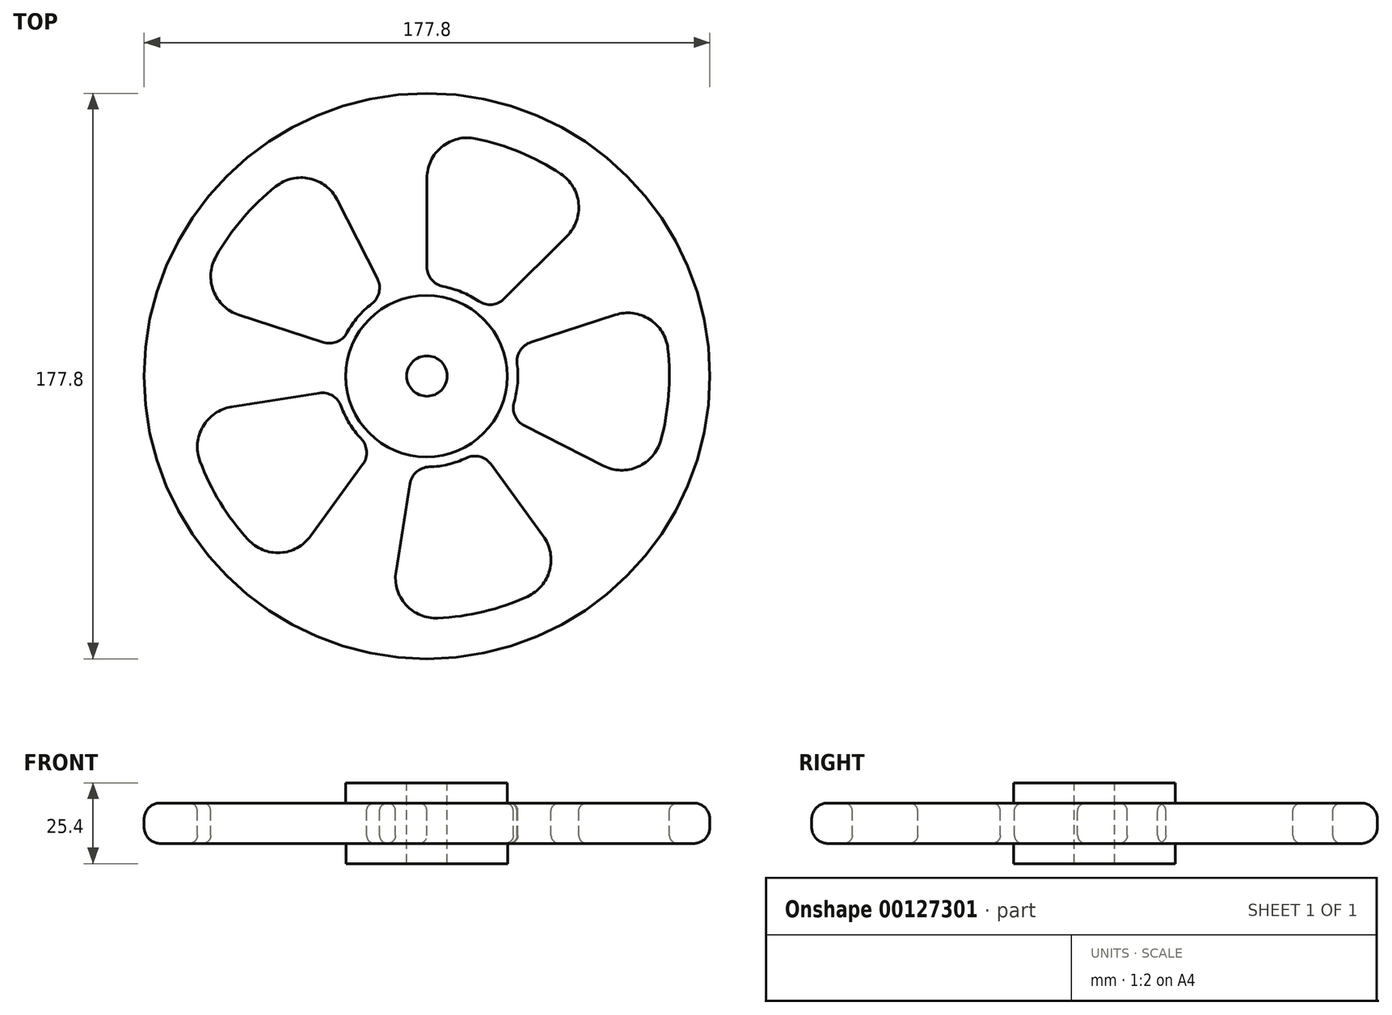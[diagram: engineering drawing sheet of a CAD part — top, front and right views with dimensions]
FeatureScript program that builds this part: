
annotation { "Feature Type Name" : "Feature", "Feature Type Description" : "" }
export const myFeature = defineFeature(function(context is Context, id is Id, definition is map)
    precondition{}
    {
        {
            var Q0;
            Q0=qCreatedBy(makeId("Top.planeOp"),FACE);
            var sketch = newSketch(context, id + "F0", { "sketchPlane" : qUnion([Q0])});
            skCircle(sketch, "E0", {"center": v(0, 0) * mm, "radius": 88.9 * mm});
            skSolve(sketch);
        }
        {
            var Q0;
            Q0 = qSketchRegion(id + "F0", true);
            extrude(context, id + "F1", {"entities" : qUnion([Q0]), "depth" : 12.7 * mm});
        }
        {
            var Q0;
            Q0=makeQuery(id+"F1.opExtrude","CAP_FACE",FACE,{"disambiguationData":[OSD([sQuery(id+"F0.wireOp",EDGE,"E0")])],"isStart":false});
            var sketch = newSketch(context, id + "F2", { "sketchPlane" : qUnion([Q0])});
            skCircle(sketch, "E1", {"center": v(-0.17, -0.07) * mm, "radius": 25.4 * mm});
            skSolve(sketch);
        }
        {
            var Q0;
            Q0 = qSketchRegion(id + "F2", true);
            extrude(context, id + "F3", {"entities" : qUnion([Q0]), "operationType" : NewBodyOperationType.ADD, "depth" : 6.35 * mm});
        }
        {
            var Q0;
            Q0=makeQuery(id+"F1.opExtrude","CAP_FACE",FACE,{"disambiguationData":[OSD([sQuery(id+"F0.wireOp",EDGE,"E0")])],"isStart":true});
            var sketch = newSketch(context, id + "F4", { "sketchPlane" : qUnion([Q0])});
            skCircle(sketch, "E2", {"center": v(0, 0) * mm, "radius": 25.4 * mm});
            skSolve(sketch);
        }
        {
            var Q0;
            Q0 = qSketchRegion(id + "F4", true);
            var Q1;
            Q1=makeQuery(id+"F4.imprint","IMPRINT",FACE,{"disambiguationData":[TD([[makeQuery(id+"F4.imprint","IMPRINT",EDGE,{"derivedFrom":sQuery(id+"F4.wireOp",EDGE,"E2")}),1.0]])]});
            extrude(context, id + "F5", {"entities" : qUnion([Q0, Q1]), "operationType" : NewBodyOperationType.ADD, "depth" : 6.35 * mm});
        }
        {
            var Q0;
            Q0=makeQuery(id+"F3.opExtrude","CAP_FACE",FACE,{"disambiguationData":[OSD([sQuery(id+"F2.wireOp",EDGE,"E1")])],"isStart":false});
            var sketch = newSketch(context, id + "F6", { "sketchPlane" : qUnion([Q0])});
            skArc(sketch, "E3", {"start": v(16.2, 23.54) * mm, "mid": v(10.94, 26.4) * mm, "end": v(5.2, 28.1) * mm});
            skArc(sketch, "E4", {"start": v(42.02, 63.57) * mm, "mid": v(29.16, 70.4) * mm, "end": v(15.24, 74.66) * mm});
            skLineSegment(sketch, "E5", {"start": v(0, 0) * mm, "end": v(0, 83.16) * mm, "construction": true});
            skLineSegment(sketch, "E6", {"start": v(0, 0) * mm, "end": v(59.56, 59.56) * mm, "construction": true});
            skLineSegment(sketch, "E7", {"start": v(0, 0) * mm, "end": v(80.55, 0) * mm, "construction": true});
            skLineSegment(sketch, "E8", {"start": v(24.28, 24.28) * mm, "end": v(44, 44) * mm});
            skLineSegment(sketch, "E9", {"start": v(0, 34.34) * mm, "end": v(0, 62.22) * mm});
            skPoint(sketch, "E10.visualSharp", {"position": v(0, 76.2) * mm});
            skArc(sketch, "E10.filletArc", {"start": v(15.24, 74.66) * mm, "mid": v(4.67, 72.05) * mm, "end": v(0, 62.22) * mm});
            skPoint(sketch, "E11.visualSharp", {"position": v(53.88, 53.88) * mm});
            skArc(sketch, "E11.filletArc", {"start": v(44, 44) * mm, "mid": v(47.65, 54.25) * mm, "end": v(42.02, 63.57) * mm});
            skPoint(sketch, "E12.visualSharp", {"position": v(0, 28.58) * mm});
            skArc(sketch, "E12.filletArc", {"start": v(0, 34.34) * mm, "mid": v(1.47, 30.28) * mm, "end": v(5.2, 28.1) * mm});
            skPoint(sketch, "E13.visualSharp", {"position": v(20.2, 20.2) * mm});
            skArc(sketch, "E13.filletArc", {"start": v(16.2, 23.54) * mm, "mid": v(20.37, 22.45) * mm, "end": v(24.28, 24.28) * mm});
            skLineSegment(sketch, "E14.1.0", {"start": v(-15.6, 30.6) * mm, "end": v(-28.25, 55.44) * mm});
            skArc(sketch, "E14.1.1", {"start": v(-28.25, 55.44) * mm, "mid": v(-36.87, 62.08) * mm, "end": v(-47.47, 59.6) * mm});
            skArc(sketch, "E14.1.2", {"start": v(-47.47, 59.6) * mm, "mid": v(-57.94, 49.49) * mm, "end": v(-66.3, 37.57) * mm});
            skArc(sketch, "E14.1.3", {"start": v(-66.3, 37.57) * mm, "mid": v(-67.09, 26.7) * mm, "end": v(-59.17, 19.23) * mm});
            skLineSegment(sketch, "E14.1.4", {"start": v(-32.66, 10.61) * mm, "end": v(-59.17, 19.23) * mm});
            skArc(sketch, "E14.1.5", {"start": v(-32.66, 10.61) * mm, "mid": v(-28.35, 10.75) * mm, "end": v(-25.12, 13.62) * mm});
            skArc(sketch, "E14.1.6", {"start": v(-17.39, 22.68) * mm, "mid": v(-21.73, 18.56) * mm, "end": v(-25.12, 13.62) * mm});
            skArc(sketch, "E14.1.7", {"start": v(-17.39, 22.68) * mm, "mid": v(-15.06, 26.31) * mm, "end": v(-15.6, 30.6) * mm});
            skLineSegment(sketch, "E14.2.0", {"start": v(-33.92, -5.37) * mm, "end": v(-61.45, -9.73) * mm});
            skArc(sketch, "E14.2.1", {"start": v(-61.45, -9.73) * mm, "mid": v(-70.44, -15.88) * mm, "end": v(-71.36, -26.73) * mm});
            skArc(sketch, "E14.2.2", {"start": v(-71.36, -26.73) * mm, "mid": v(-64.97, -39.81) * mm, "end": v(-56.21, -51.44) * mm});
            skArc(sketch, "E14.2.3", {"start": v(-56.21, -51.44) * mm, "mid": v(-46.13, -55.55) * mm, "end": v(-36.57, -50.33) * mm});
            skLineSegment(sketch, "E14.2.4", {"start": v(-20.19, -27.78) * mm, "end": v(-36.57, -50.33) * mm});
            skArc(sketch, "E14.2.5", {"start": v(-20.19, -27.78) * mm, "mid": v(-18.99, -23.63) * mm, "end": v(-20.72, -19.68) * mm});
            skArc(sketch, "E14.2.6", {"start": v(-26.94, -9.53) * mm, "mid": v(-24.36, -14.93) * mm, "end": v(-20.72, -19.68) * mm});
            skArc(sketch, "E14.2.7", {"start": v(-26.94, -9.53) * mm, "mid": v(-29.68, -6.19) * mm, "end": v(-33.92, -5.37) * mm});
            skLineSegment(sketch, "E15.1.3.0", {"start": v(-5.37, -33.92) * mm, "end": v(-9.73, -61.45) * mm});
            skArc(sketch, "E15.3.3.0", {"start": v(-9.73, -61.45) * mm, "mid": v(-6.66, -71.9) * mm, "end": v(3.37, -76.13) * mm});
            skArc(sketch, "E15.7.3.0", {"start": v(3.37, -76.13) * mm, "mid": v(17.79, -74.1) * mm, "end": v(31.55, -69.36) * mm});
            skArc(sketch, "E15.11.3.0", {"start": v(31.55, -69.36) * mm, "mid": v(38.58, -61.04) * mm, "end": v(36.57, -50.33) * mm});
            skLineSegment(sketch, "E15.15.3.0", {"start": v(20.19, -27.78) * mm, "end": v(36.57, -50.33) * mm});
            skArc(sketch, "E15.18.3.0", {"start": v(20.19, -27.78) * mm, "mid": v(16.61, -25.36) * mm, "end": v(12.31, -25.79) * mm});
            skArc(sketch, "E15.22.3.0", {"start": v(0.74, -28.57) * mm, "mid": v(6.67, -27.79) * mm, "end": v(12.31, -25.79) * mm});
            skArc(sketch, "E15.26.3.0", {"start": v(0.74, -28.57) * mm, "mid": v(-3.29, -30.14) * mm, "end": v(-5.37, -33.92) * mm});
            skLineSegment(sketch, "E15.1.4.0", {"start": v(30.6, -15.6) * mm, "end": v(55.44, -28.25) * mm});
            skArc(sketch, "E15.3.4.0", {"start": v(55.44, -28.25) * mm, "mid": v(66.32, -28.55) * mm, "end": v(73.44, -20.32) * mm});
            skArc(sketch, "E15.7.4.0", {"start": v(73.44, -20.32) * mm, "mid": v(75.97, -5.98) * mm, "end": v(75.72, 8.58) * mm});
            skArc(sketch, "E15.11.4.0", {"start": v(75.72, 8.58) * mm, "mid": v(69.97, 17.83) * mm, "end": v(59.17, 19.23) * mm});
            skLineSegment(sketch, "E15.15.4.0", {"start": v(32.66, 10.61) * mm, "end": v(59.17, 19.23) * mm});
            skArc(sketch, "E15.18.4.0", {"start": v(32.66, 10.61) * mm, "mid": v(29.25, 7.96) * mm, "end": v(28.33, 3.74) * mm});
            skArc(sketch, "E15.22.4.0", {"start": v(27.4, -8.13) * mm, "mid": v(28.49, -2.24) * mm, "end": v(28.33, 3.74) * mm});
            skArc(sketch, "E15.26.4.0", {"start": v(27.4, -8.13) * mm, "mid": v(27.65, -12.44) * mm, "end": v(30.6, -15.6) * mm});
            skSolve(sketch);
        }
        {
            var Q0;
            Q0 = qSketchRegion(id + "F6", true);
            extrude(context, id + "F7", {"entities" : qUnion([Q0]), "operationType" : NewBodyOperationType.REMOVE, "endBound" : BoundingType.THROUGH_ALL, "oppositeDirection" : true, "depth" : 25.4 * mm});
        }
        {
            var Q0;
            Q0=makeQuery(id+"F3.opExtrude","CAP_FACE",FACE,{"disambiguationData":[OSD([sQuery(id+"F2.wireOp",EDGE,"E1")])],"isStart":false});
            var sketch = newSketch(context, id + "F8", { "sketchPlane" : qUnion([Q0])});
            skCircle(sketch, "E16", {"center": v(0, 0) * mm, "radius": 6.35 * mm});
            skSolve(sketch);
        }
        {
            var Q0;
            Q0 = qSketchRegion(id + "F8", true);
            extrude(context, id + "F9", {"entities" : qUnion([Q0]), "operationType" : NewBodyOperationType.REMOVE, "endBound" : BoundingType.THROUGH_ALL, "oppositeDirection" : true, "depth" : 25.4 * mm});
        }
        {
            var Q0;
            Q0=makeQuery(id+"F1.opExtrude","SWEPT_FACE",FACE,{"disambiguationData":[OSD([sQuery(id+"F0.wireOp",EDGE,"E0")])]});
            fillet(context, id + "F10", {"entities" : qUnion([Q0]), "radius" : 5.08 * mm, "tangentPropagation" : true, "allowEdgeOverflow" : false});
        }
        {
            var Q0;
            Q0=makeQuery(id+"F7.boolean.opBoolean","COPY",FACE,{"derivedFrom":makeQuery(id+"F7.opExtrude","SWEPT_FACE",FACE,{"disambiguationData":[OSD([sQuery(id+"F6.wireOp",EDGE,"E15.15.4.0")])]})});
            var Q1;
            Q1=makeQuery(id+"F7.boolean.opBoolean","COPY",FACE,{"derivedFrom":makeQuery(id+"F7.opExtrude","SWEPT_FACE",FACE,{"disambiguationData":[OSD([sQuery(id+"F6.wireOp",EDGE,"E9")])]})});
            var Q2;
            Q2=makeQuery(id+"F7.boolean.opBoolean","COPY",FACE,{"derivedFrom":makeQuery(id+"F7.opExtrude","SWEPT_FACE",FACE,{"disambiguationData":[OSD([sQuery(id+"F6.wireOp",EDGE,"E14.1.2")])]})});
            var Q3;
            Q3=makeQuery(id+"F7.boolean.opBoolean","COPY",FACE,{"derivedFrom":makeQuery(id+"F7.opExtrude","SWEPT_FACE",FACE,{"disambiguationData":[OSD([sQuery(id+"F6.wireOp",EDGE,"E14.2.0")])]})});
            var Q4;
            Q4=makeQuery(id+"F7.boolean.opBoolean","COPY",FACE,{"derivedFrom":makeQuery(id+"F7.opExtrude","SWEPT_FACE",FACE,{"disambiguationData":[OSD([sQuery(id+"F6.wireOp",EDGE,"E15.1.3.0")])]})});
            fillet(context, id + "F11", {"entities" : qUnion([Q0, Q1, Q2, Q3, Q4]), "radius" : 2.54 * mm, "tangentPropagation" : true, "allowEdgeOverflow" : false});
        }
    });
